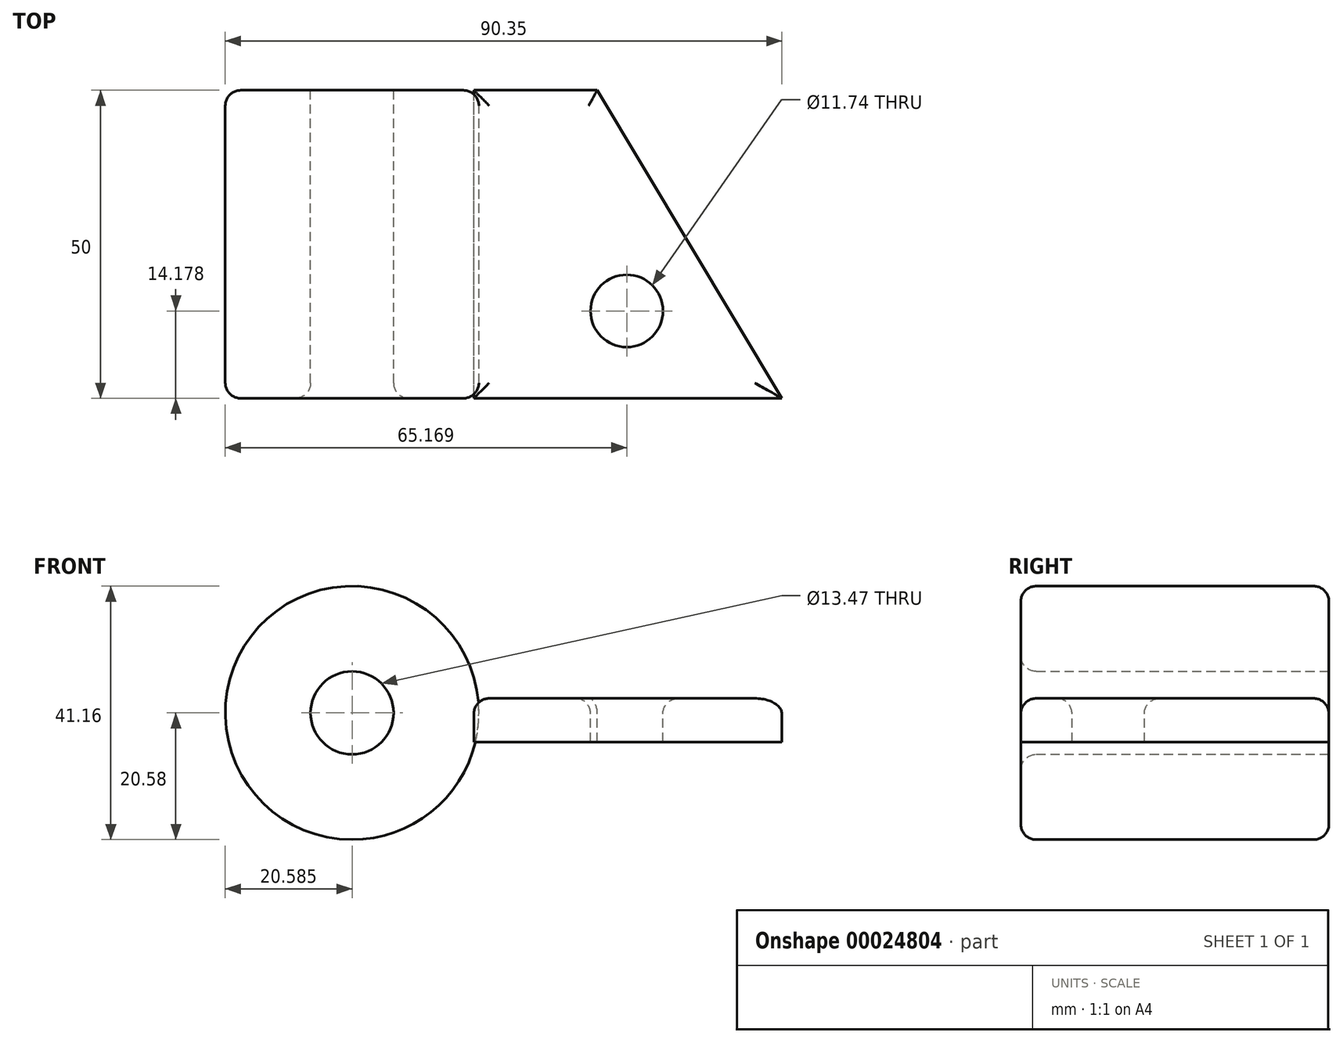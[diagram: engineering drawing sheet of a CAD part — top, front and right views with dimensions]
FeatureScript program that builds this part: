
annotation { "Feature Type Name" : "Feature", "Feature Type Description" : "" }
export const myFeature = defineFeature(function(context is Context, id is Id, definition is map)
    precondition{}
    {
        {
            var Q0;
            Q0=qCreatedBy(makeId("Front.planeOp"),FACE);
            var sketch = newSketch(context, id + "F0", { "sketchPlane" : qUnion([Q0])});
            skCircle(sketch, "E0", {"center": v(-44.76, 6.82) * mm, "radius": 20.58 * mm});
            skCircle(sketch, "E1", {"center": v(-44.76, 6.82) * mm, "radius": 6.74 * mm});
            skSolve(sketch);
        }
        {
            var Q0;
            Q0=makeQuery(id+"F0.imprint","IMPRINT",FACE,{"disambiguationData":[TD([[makeQuery(id+"F0.imprint","IMPRINT",EDGE,{"derivedFrom":sQuery(id+"F0.wireOp",EDGE,"E0")}),1.0]])]});
            extrude(context, id + "F1", {"entities" : qUnion([Q0]), "depth" : 50 * mm});
        }
        {
            var Q0;
            Q0=qCreatedBy(makeId("Right.planeOp"),FACE);
            var sketch = newSketch(context, id + "F2", { "sketchPlane" : qUnion([Q0])});
            skLineSegment(sketch, "E2.bottom", {"start": v(-50.14, 9.18) * mm, "end": v(0, 9.18) * mm});
            skLineSegment(sketch, "E2.top", {"start": v(-50.14, 2.1) * mm, "end": v(0, 2.1) * mm});
            skLineSegment(sketch, "E2.left", {"start": v(-50.14, 9.18) * mm, "end": v(-50.14, 2.1) * mm});
            skLineSegment(sketch, "E2.right", {"start": v(0, 9.18) * mm, "end": v(0, 2.1) * mm});
            skSolve(sketch);
        }
        {
            var Q0;
            Q0=makeQuery(id+"F2.imprint","IMPRINT",FACE,{"disambiguationData":[TD([[makeQuery(id+"F2.imprint","IMPRINT",EDGE,{"derivedFrom":sQuery(id+"F2.wireOp",EDGE,"E2.bottom")}),-1.0]])]});
            extrude(context, id + "F3", {"entities" : qUnion([Q0]), "oppositeDirection" : true, "depth" : 25 * mm});
        }
        {
            var Q0;
            Q0=makeQuery(id+"F3.opExtrude","CAP_FACE",FACE,{"disambiguationData":[OSD([sQuery(id+"F2.wireOp",EDGE,"E2.bottom"),sQuery(id+"F2.wireOp",EDGE,"E2.top"),sQuery(id+"F2.wireOp",EDGE,"E2.left"),sQuery(id+"F2.wireOp",EDGE,"E2.right")])],"isStart":true});
            extrude(context, id + "F4", {"entities" : qUnion([Q0]), "operationType" : NewBodyOperationType.ADD, "depth" : 25 * mm});
        }
        {
            var Q0;
            {var subQ0=sQuery(id+"F2.wireOp",EDGE,"E2.left");Q0=makeQuery(id+"F4.boolean.opBoolean","MERGE",FACE,{"derivedFrom":[makeQuery(id+"F3.opExtrude","SWEPT_FACE",FACE,{"disambiguationData":[OSD([subQ0])]}),makeQuery(id+"F4.opExtrude","SWEPT_FACE",FACE,{"disambiguationData":[OSD([subQ0])]})]});}
            var Q1;
            Q1=makeQuery(id+"F1.opExtrude","CAP_FACE",FACE,{"disambiguationData":[OSD([sQuery(id+"F0.wireOp",EDGE,"E0"),sQuery(id+"F0.wireOp",EDGE,"E1")])],"isStart":false});
            extrude(context, id + "F5", {"entities" : qUnion([Q0]), "operationType" : NewBodyOperationType.REMOVE, "endBound" : BoundingType.UP_TO_SURFACE, "oppositeDirection" : true, "endBoundEntityFace" : qUnion([Q1]), "depth" : 25 * mm});
        }
        {
            var Q0;
            {var subQ0=sQuery(id+"F2.wireOp",EDGE,"E2.bottom");Q0=makeQuery(id+"F4.boolean.opBoolean","MERGE",FACE,{"derivedFrom":[makeQuery(id+"F3.opExtrude","SWEPT_FACE",FACE,{"disambiguationData":[OSD([subQ0])]}),makeQuery(id+"F4.opExtrude","SWEPT_FACE",FACE,{"disambiguationData":[OSD([subQ0])]})]});}
            var sketch = newSketch(context, id + "F6", { "sketchPlane" : qUnion([Q0])});
            skLineSegment(sketch, "E3", {"start": v(25, -50) * mm, "end": v(-4.96, 0) * mm});
            skSolve(sketch);
        }
        {
            var Q0;
            {var subQ3=sQuery(id+"F6.wireOp",EDGE,"E3");Q0=makeQuery(id+"F6.imprint","IMPRINT",FACE,{"disambiguationData":[TD([[makeQuery(id+"F6.imprint","IMPRINT",EDGE,{"derivedFrom":subQ3}),-1.0]])]});}
            extrude(context, id + "F7", {"entities" : qUnion([Q0]), "operationType" : NewBodyOperationType.REMOVE, "endBound" : BoundingType.THROUGH_ALL, "oppositeDirection" : true, "depth" : 25 * mm});
        }
        {
            var Q0;
            {var subQ0=sQuery(id+"F2.wireOp",EDGE,"E2.bottom");Q0=makeQuery(id+"F4.boolean.opBoolean","MERGE",FACE,{"derivedFrom":[makeQuery(id+"F3.opExtrude","SWEPT_FACE",FACE,{"disambiguationData":[OSD([subQ0])]}),makeQuery(id+"F4.opExtrude","SWEPT_FACE",FACE,{"disambiguationData":[OSD([subQ0])]})]});}
            var sketch = newSketch(context, id + "F8", { "sketchPlane" : qUnion([Q0])});
            skCircle(sketch, "E4", {"center": v(-0.18, -35.82) * mm, "radius": 5.87 * mm});
            skSolve(sketch);
        }
        {
            var Q0;
            Q0=makeQuery(id+"F8.imprint","IMPRINT",FACE,{"disambiguationData":[TD([[makeQuery(id+"F8.imprint","IMPRINT",EDGE,{"derivedFrom":sQuery(id+"F8.wireOp",EDGE,"E4")}),1.0]])]});
            extrude(context, id + "F9", {"entities" : qUnion([Q0]), "operationType" : NewBodyOperationType.REMOVE, "endBound" : BoundingType.THROUGH_ALL, "oppositeDirection" : true, "depth" : 25 * mm});
        }
        {
            var Q0;
            Q0=makeQuery(id+"F1.opExtrude","SWEPT_FACE",FACE,{"disambiguationData":[OSD([sQuery(id+"F0.wireOp",EDGE,"E0")])]});
            var Q1;
            {var subQ0=sQuery(id+"F2.wireOp",EDGE,"E2.bottom");Q1=makeQuery(id+"F4.boolean.opBoolean","MERGE",FACE,{"derivedFrom":[makeQuery(id+"F3.opExtrude","SWEPT_FACE",FACE,{"disambiguationData":[OSD([subQ0])]}),makeQuery(id+"F4.opExtrude","SWEPT_FACE",FACE,{"disambiguationData":[OSD([subQ0])]})]});}
            var Q2;
            Q2=makeQuery(id+"F5.boolean.opBoolean","MERGE",FACE,{"derivedFrom":[makeQuery(id+"F1.opExtrude","CAP_FACE",FACE,{"disambiguationData":[OSD([sQuery(id+"F0.wireOp",EDGE,"E0"),sQuery(id+"F0.wireOp",EDGE,"E1")])],"isStart":false}),makeQuery(id+"F5.opExtrude","CAP_FACE",FACE,{"disambiguationData":[OSD([sQuery(id+"F2.wireOp",EDGE,"E2.left")])],"isStart":false})]});
            fillet(context, id + "F10", {"entities" : qUnion([Q0, Q1, Q2]), "radius" : 2.5 * mm, "tangentPropagation" : true, "allowEdgeOverflow" : false});
        }
    });
